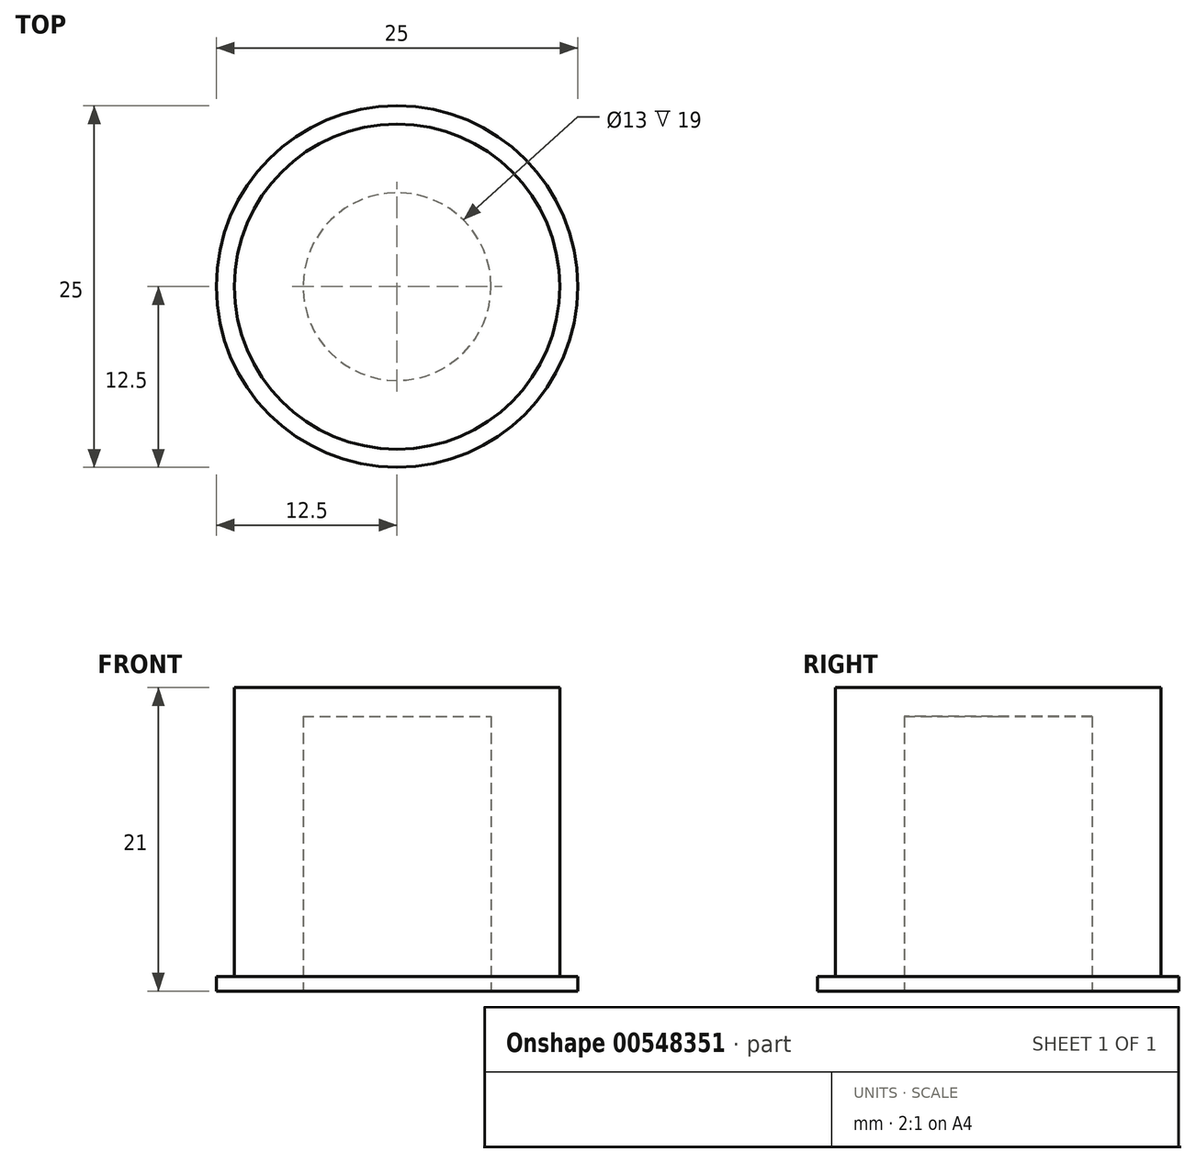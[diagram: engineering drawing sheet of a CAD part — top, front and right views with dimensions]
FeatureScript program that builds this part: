
annotation { "Feature Type Name" : "Feature", "Feature Type Description" : "" }
export const myFeature = defineFeature(function(context is Context, id is Id, definition is map)
    precondition{}
    {
        {
            var Q0;
            Q0=qCreatedBy(makeId("Top.planeOp"),FACE);
            var sketch = newSketch(context, id + "F0", { "sketchPlane" : qUnion([Q0])});
            skCircle(sketch, "E0", {"center": v(0, 0) * mm, "radius": 11.25 * mm});
            skCircle(sketch, "E1", {"center": v(0, 0) * mm, "radius": 12.5 * mm});
            skSolve(sketch);
        }
        {
            var Q0;
            Q0=makeQuery(id+"F0.imprint","IMPRINT",FACE,{"disambiguationData":[TD([[makeQuery(id+"F0.imprint","IMPRINT",EDGE,{"derivedFrom":sQuery(id+"F0.wireOp",EDGE,"E0")}),1.0]])]});
            extrude(context, id + "F1", {"entities" : qUnion([Q0]), "depth" : 21 * mm, "offsetDistance" : 25 * mm});
        }
        {
            var Q0;
            Q0=qSketchRegion(id+"F0",true);
            extrude(context, id + "F2", {"entities" : qUnion([Q0]), "operationType" : NewBodyOperationType.ADD, "depth" : 1 * mm, "offsetDistance" : 25 * mm});
        }
        {
            var Q0;
            {var subQ0=sQuery(id+"F0.wireOp",EDGE,"E0");Q0=makeQuery(id+"F2.boolean.opBoolean","MERGE",FACE,{"derivedFrom":[makeQuery(id+"F1.opExtrude","CAP_FACE",FACE,{"disambiguationData":[OSD([subQ0])],"isStart":true}),makeQuery(id+"F2.opExtrude","CAP_FACE",FACE,{"disambiguationData":[OSD([subQ0,sQuery(id+"F0.wireOp",EDGE,"E1")])],"isStart":true})]});}
            var sketch = newSketch(context, id + "F3", { "sketchPlane" : qUnion([Q0])});
            skCircle(sketch, "E2", {"center": v(0, 0) * mm, "radius": 6.5 * mm});
            skSolve(sketch);
        }
        {
            var Q0;
            Q0=makeQuery(id+"F3.imprint","IMPRINT",FACE,{"disambiguationData":[TD([[makeQuery(id+"F3.imprint","IMPRINT",EDGE,{"derivedFrom":sQuery(id+"F3.wireOp",EDGE,"E2")}),1.0]])]});
            extrude(context, id + "F4", {"entities" : qUnion([Q0]), "operationType" : NewBodyOperationType.REMOVE, "oppositeDirection" : true, "depth" : 19 * mm, "offsetDistance" : 25 * mm});
        }
    });
